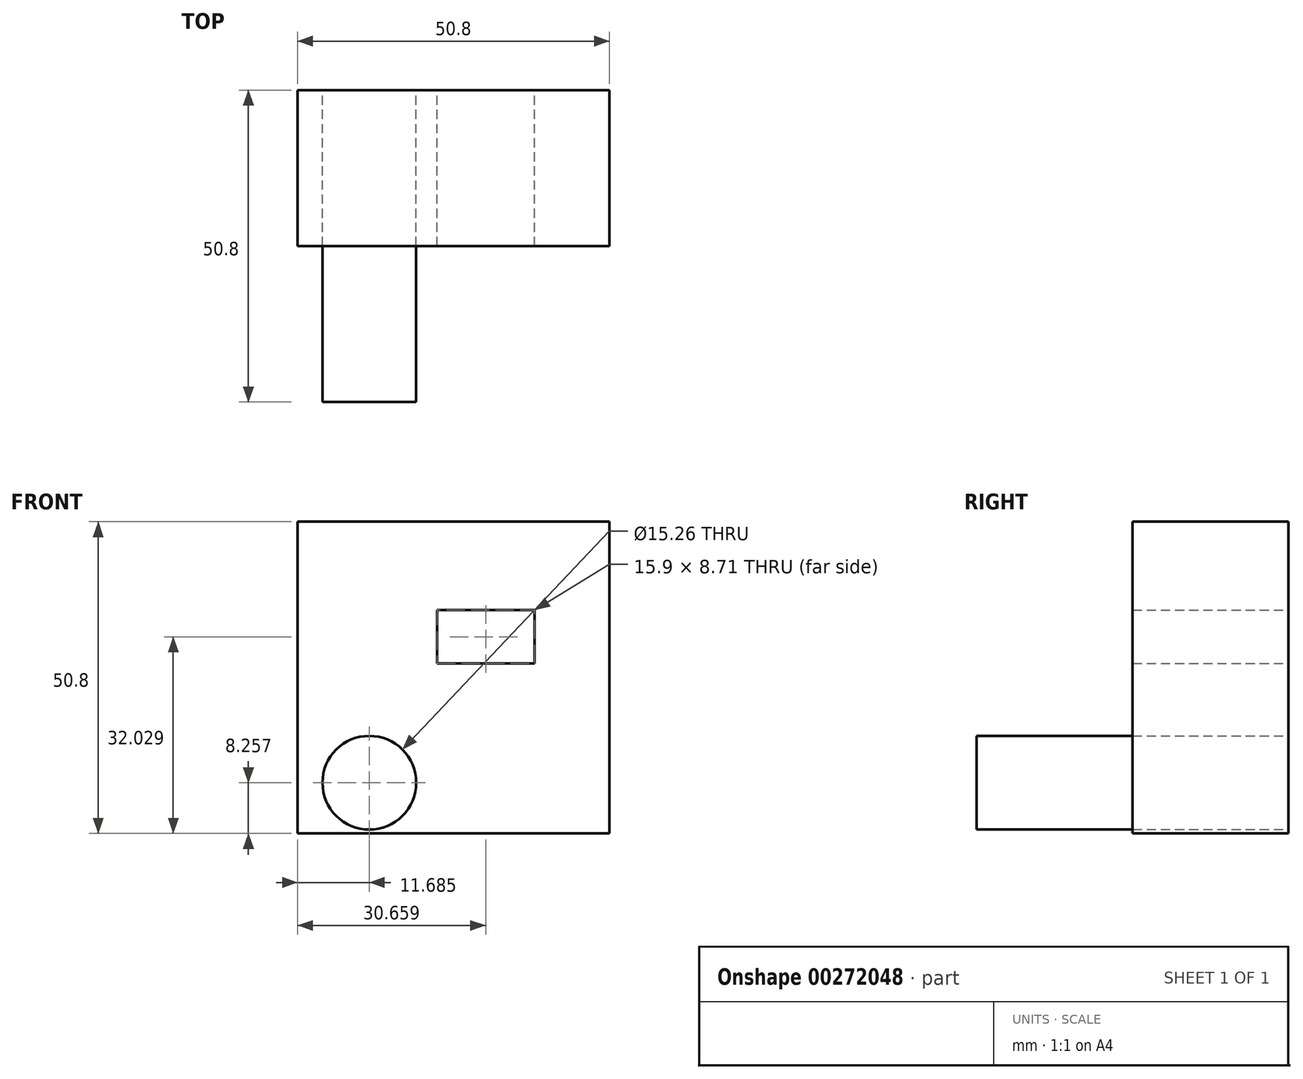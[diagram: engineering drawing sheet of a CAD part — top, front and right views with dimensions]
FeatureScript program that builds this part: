
annotation { "Feature Type Name" : "Feature", "Feature Type Description" : "" }
export const myFeature = defineFeature(function(context is Context, id is Id, definition is map)
    precondition{}
    {
        {
            var Q0;
            Q0=qCreatedBy(makeId("Front.planeOp"),FACE);
            var sketch = newSketch(context, id + "F0", { "sketchPlane" : qUnion([Q0])});
            skLineSegment(sketch, "E0.bottom", {"start": v(-77, -77.14) * mm, "end": v(-26.2, -77.14) * mm});
            skLineSegment(sketch, "E0.top", {"start": v(-77, -26.34) * mm, "end": v(-26.2, -26.34) * mm});
            skLineSegment(sketch, "E0.left", {"start": v(-77, -77.14) * mm, "end": v(-77, -26.34) * mm});
            skLineSegment(sketch, "E0.right", {"start": v(-26.2, -77.14) * mm, "end": v(-26.2, -26.34) * mm});
            skCircle(sketch, "E1", {"center": v(-65.3, -68.88) * mm, "radius": 7.63 * mm});
            skLineSegment(sketch, "E2.bottom", {"start": v(-54.28, -40.75) * mm, "end": v(-38.38, -40.75) * mm});
            skLineSegment(sketch, "E2.top", {"start": v(-54.28, -49.47) * mm, "end": v(-38.38, -49.47) * mm});
            skLineSegment(sketch, "E2.left", {"start": v(-54.28, -40.75) * mm, "end": v(-54.28, -49.47) * mm});
            skLineSegment(sketch, "E2.right", {"start": v(-38.38, -40.75) * mm, "end": v(-38.38, -49.47) * mm});
            skSolve(sketch);
        }
        {
            var Q0;
            Q0=makeQuery(id+"F0.imprint","IMPRINT",FACE,{"disambiguationData":[TD([[makeQuery(id+"F0.imprint","IMPRINT",EDGE,{"derivedFrom":sQuery(id+"F0.wireOp",EDGE,"E2.bottom")}),-1.0]])]});
            extrude(context, id + "F1", {"entities" : qUnion([Q0]), "depth" : 25.4 * mm});
        }
        {
            var Q0;
            Q0=makeQuery(id+"F0.imprint","IMPRINT",FACE,{"disambiguationData":[TD([[makeQuery(id+"F0.imprint","IMPRINT",EDGE,{"derivedFrom":sQuery(id+"F0.wireOp",EDGE,"E1")}),1.0]])]});
            extrude(context, id + "F2", {"entities" : qUnion([Q0]), "depth" : 50.8 * mm});
        }
        {
            var Q0;
            Q0=makeQuery(id+"F0.imprint","IMPRINT",FACE,{"disambiguationData":[TD([[makeQuery(id+"F0.imprint","IMPRINT",EDGE,{"derivedFrom":sQuery(id+"F0.wireOp",EDGE,"E0.bottom")}),1.0]])]});
            extrude(context, id + "F3", {"entities" : qUnion([Q0]), "depth" : 25.4 * mm});
        }
    });
